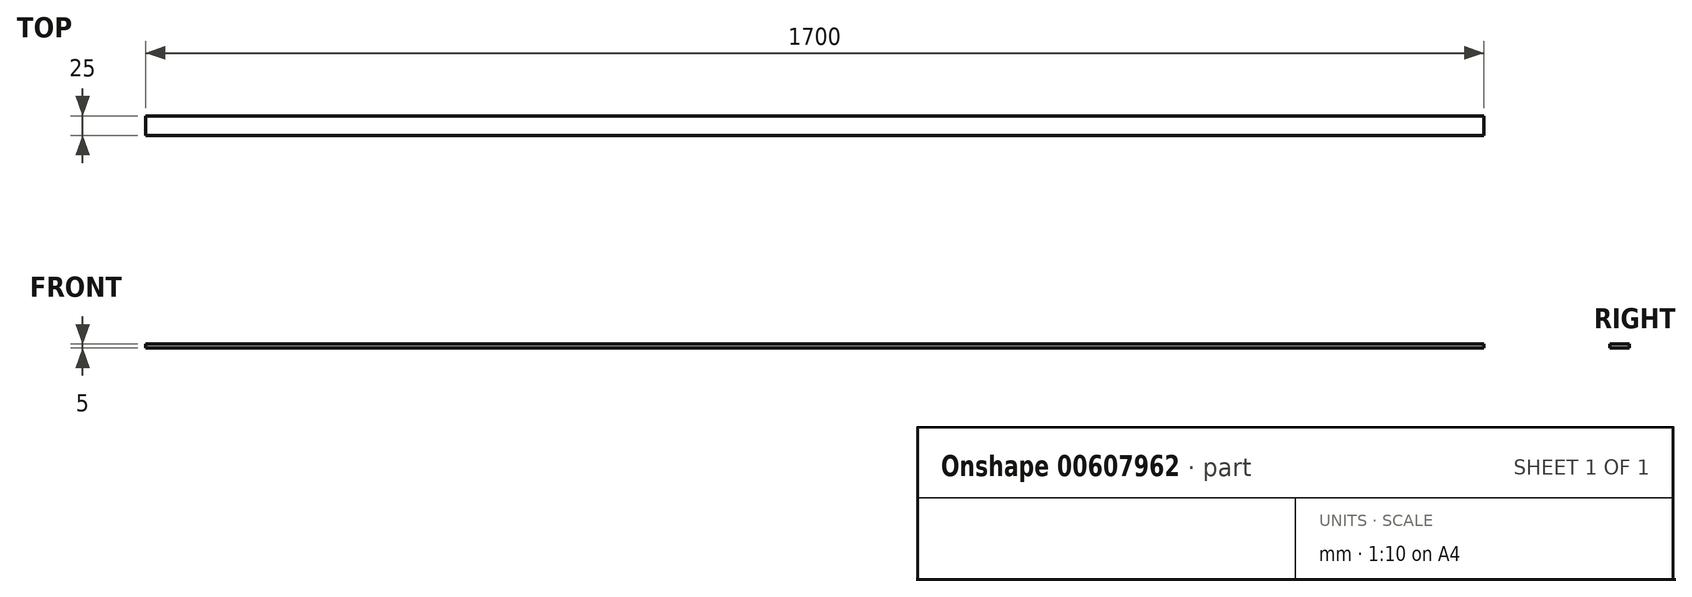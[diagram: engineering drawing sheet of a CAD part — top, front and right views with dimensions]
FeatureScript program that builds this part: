
annotation { "Feature Type Name" : "Feature", "Feature Type Description" : "" }
export const myFeature = defineFeature(function(context is Context, id is Id, definition is map)
    precondition{}
    {
        {
            var Q0;
            Q0=qCreatedBy(makeId("Front.planeOp"),FACE);
            var sketch = newSketch(context, id + "F0", { "sketchPlane" : qUnion([Q0])});
            skLineSegment(sketch, "E0.bottom", {"start": v(-850.34, -123.52) * mm, "end": v(849.66, -123.52) * mm});
            skLineSegment(sketch, "E0.top", {"start": v(-850.34, -128.52) * mm, "end": v(849.66, -128.52) * mm});
            skLineSegment(sketch, "E0.left", {"start": v(-850.34, -123.52) * mm, "end": v(-850.34, -128.52) * mm});
            skLineSegment(sketch, "E0.right", {"start": v(849.66, -123.52) * mm, "end": v(849.66, -128.52) * mm});
            skSolve(sketch);
        }
        {
            var Q0;
            Q0 = qSketchRegion(id + "F0", true);
            extrude(context, id + "F1", {"entities" : qUnion([Q0]), "depth" : 25 * mm, "offsetDistance" : 25 * mm});
        }
    });
